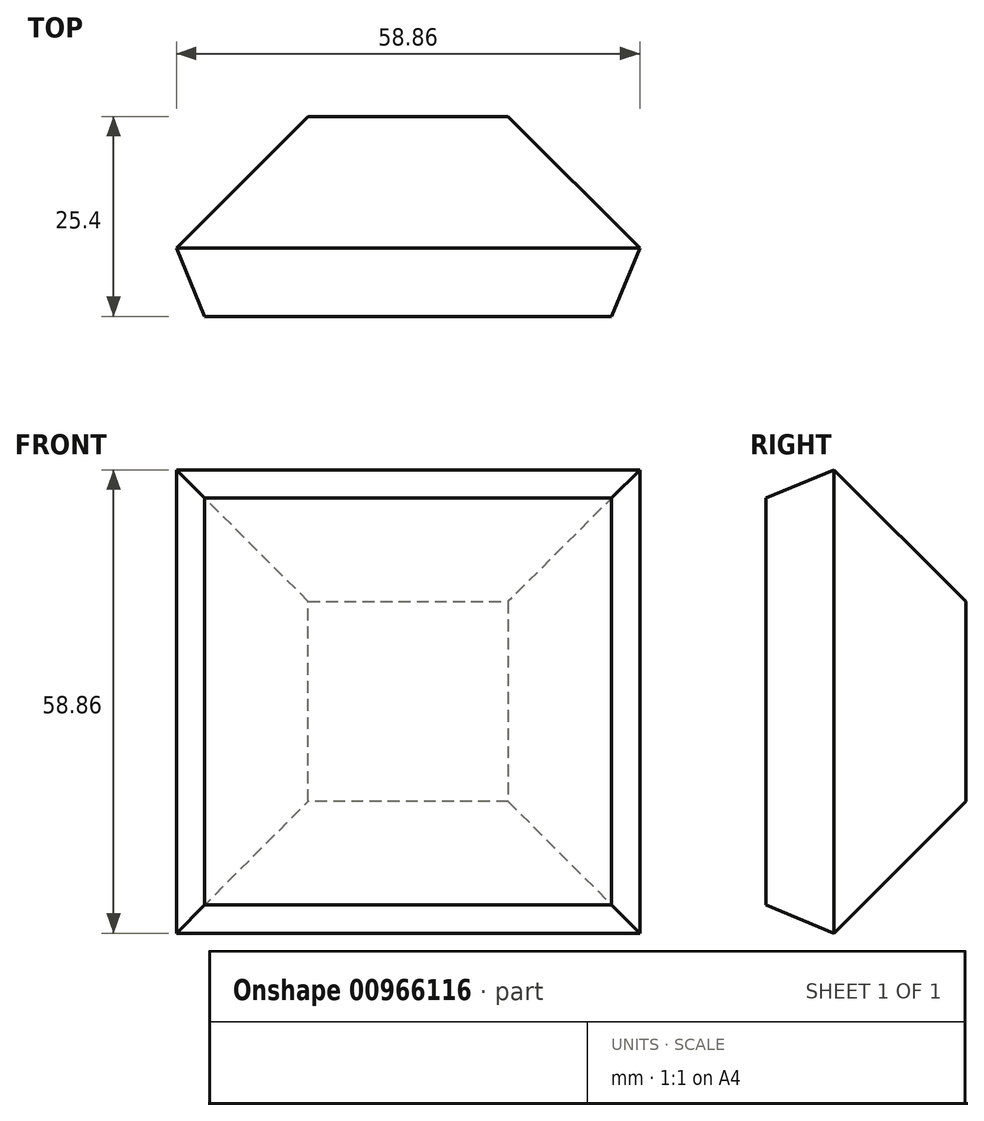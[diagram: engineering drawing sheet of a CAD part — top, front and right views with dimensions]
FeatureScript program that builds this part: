
annotation { "Feature Type Name" : "Feature", "Feature Type Description" : "" }
export const myFeature = defineFeature(function(context is Context, id is Id, definition is map)
    precondition{}
    {
        {
            var Q0;
            Q0=qCreatedBy(makeId("Front.planeOp"),FACE);
            var sketch = newSketch(context, id + "F0", { "sketchPlane" : qUnion([Q0])});
            skLineSegment(sketch, "E0.bottom", {"start": v(0, 0) * mm, "end": v(-25.4, 0) * mm});
            skLineSegment(sketch, "E0.top", {"start": v(0, 25.4) * mm, "end": v(-25.4, 25.4) * mm});
            skLineSegment(sketch, "E0.left", {"start": v(0, 0) * mm, "end": v(0, 25.4) * mm});
            skLineSegment(sketch, "E0.right", {"start": v(-25.4, 0) * mm, "end": v(-25.4, 25.4) * mm});
            skSolve(sketch);
        }
        {
            var Q0;
            Q0 = qSketchRegion(id + "F0", true);
            extrude(context, id + "F1", {"entities" : qUnion([Q0]), "depth" : 25.4 * mm, "offsetDistance" : 25.4 * mm, "hasDraft" : true, "draftAngle" : 45 * degree});
        }
        {
            var Q0;
            Q0=makeQuery(id+"F1.opExtrude","CAP_EDGE",EDGE,{"disambiguationData":[OSD([sQuery(id+"F0.wireOp",EDGE,"E0.bottom")])],"isStart":false});
            var Q1;
            Q1=makeQuery(id+"F1.opExtrude","CAP_EDGE",EDGE,{"disambiguationData":[OSD([sQuery(id+"F0.wireOp",EDGE,"E0.left")])],"isStart":false});
            var Q2;
            Q2=makeQuery(id+"F1.opExtrude","CAP_EDGE",EDGE,{"disambiguationData":[OSD([sQuery(id+"F0.wireOp",EDGE,"E0.top")])],"isStart":false});
            var Q3;
            Q3=makeQuery(id+"F1.opExtrude","CAP_EDGE",EDGE,{"disambiguationData":[OSD([sQuery(id+"F0.wireOp",EDGE,"E0.right")])],"isStart":false});
            chamfer(context, id + "F2", {"entities" : qUnion([Q0, Q1, Q2, Q3]), "width" : 5.08 * mm, "tangentPropagation" : true});
        }
    });
